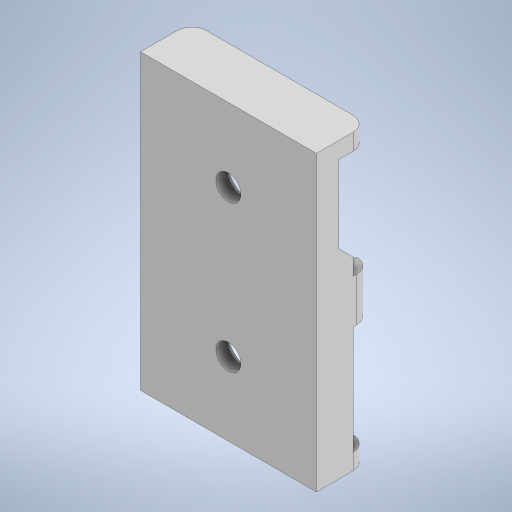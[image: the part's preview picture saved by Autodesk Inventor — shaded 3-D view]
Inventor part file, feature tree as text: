
AUTODESK INVENTOR PART (.ipt)
format: ipt  version: 2024 (Build 280153000, 153)  size: 340,480 bytes
history: native  units: mm
features: sketch x9, extrude x8, chamfer x1, fillet x1, hole x1
ambient origin geometry x8: Origin, YZ Plane, XZ Plane, XY Plane, X Axis, Y Axis, Z Axis, Center Point
bodies: Volumenkörper1 (feature_tree)
feature tree (20):
  extrude  "Extrusion1"  Depth=24.0mm
  extrude  "Extrusion2"  Depth=2.25mm
  extrude  "Extrusion4"  Depth=4.0mm TaperAngle=0.0deg
  extrude  "Extrusion5"  Depth=4.0mm
  extrude  "Extrusion6"  Depth=20.0mm
  extrude  "Extrusion7"  Depth=2.0mm TaperAngle=0.0deg
  extrude  "Extrusion8"  Depth=1.8mm
  extrude  "Extrusion9"  Depth=6.0mm
  chamfer  "Fasen1"  Distance=2.5mm
  fillet  "Rundung1"  Radius=1.0mm
  hole  "Bohrung1"  [1 undecoded]
  sketch  "Skizze1"  dims[d0=40.0mm d1=24.0mm]
  sketch  "Skizze2"  dims[d2=3.0mm d3=0.0mm d4=2.25mm]
  sketch  "Skizze4"  dims[d5=2.25mm d6=4.0mm d7=0.0mm]
  sketch  "Skizze5"  dims[d25=25.0mm d26=4.0mm]
  sketch  "Skizze6"  dims[d27=4.0mm d29=20.0mm]
  sketch  "Skizze7"  dims[d30=10.0mm d31=2.0mm d32=0.0mm]
  sketch  "Skizze9"  dims[d33=3.0mm d34=1.8mm]
  sketch  "Skizze11"  dims[d35=1.8mm d36=6.0mm d37=2.5mm d38=0.0mm d39=1.0mm]
  sketch  "Skizze12"  dims[d40=1.0mm d41=0.0mm d42=1.0mm d43=1.0mm d44=10.0mm d45=0.0mm d46=1.5mm d47=0.5mm d48=0.0mm d49=0.5mm d50=10.0mm d51=0.0mm d52=2.0mm d53=2.0mm d54=45.0deg d55=2.0mm d56=4.0mm d57=4.0mm d58=20.0mm d59=3.4mm d60=6.0mm d61=6.3mm d62=2.0mm d63=90.0deg d64=8.8mm d65=20.594885mm]
note: 1 required parameter value undecoded (feature->parameter linkage not recoverable at this tier; creation-order binding heuristic only, values carry confidence <= 0.55)
